# Revit family: SpectraLoc
name_source: partatom
category: Lighting Fixtures
revit_build: Autodesk Revit 2013 (Build: 20130531_2115(x64)
units: mm (PartAtom-declared; Revit-internal decimal feet)

## types (2) — shared parameters
Backbox = Hubbell - White
Color Filter = 16777215
Default Elevation = 48 "
Description = SpectraLoc Blue Spectrum Suppression Highbau
Dimming Lamp Color Temperature Shift = <None>
Distribution = Short Wave Suppression Aisle Optics
Emit Shape Visible in Rendering = No
Emit from Rectangle Length = 23 "
Emit from Rectangle Width = 15 "
Fixture Glass = Hubbell - White Glass
Lamp = LED Lamp
Load Classification = Lighting
Manufacturer = Hubbell Industrial Lighting
Manufacturer Fax = 866-898-0131
Model = SpectraLoc
Power factor = 1
Product Documentation Link = http://cdn.hubbellindustrial.com
Product Page URL = http://www.hubbellindustrial.com
Tilt Angle = -90.00°
URL = http://www.hubbellindustrial.com
Voltage = 120 V
Warranty = Five year warranty

## per-type parameters (varying)
| type | Apparent Load | Lumen Output | Photometric Web File | Wattage Comments | Watts |
| SPL-HL-SWSA-EDU | 113 VA | High Lumen | SPL-HL-SWSA-EDU.ies | 19-69 W | 113 W |
| SPL-XL-SWSA-EDU | 175 VA | Xtra High Lumen | SPL-XL-SWSA-EDU.ies | 112.7-175.1W | 175 W |

## geometry (parser evidence)
native form markers: Sweep x4
no freeform markers — native parametric forms only
